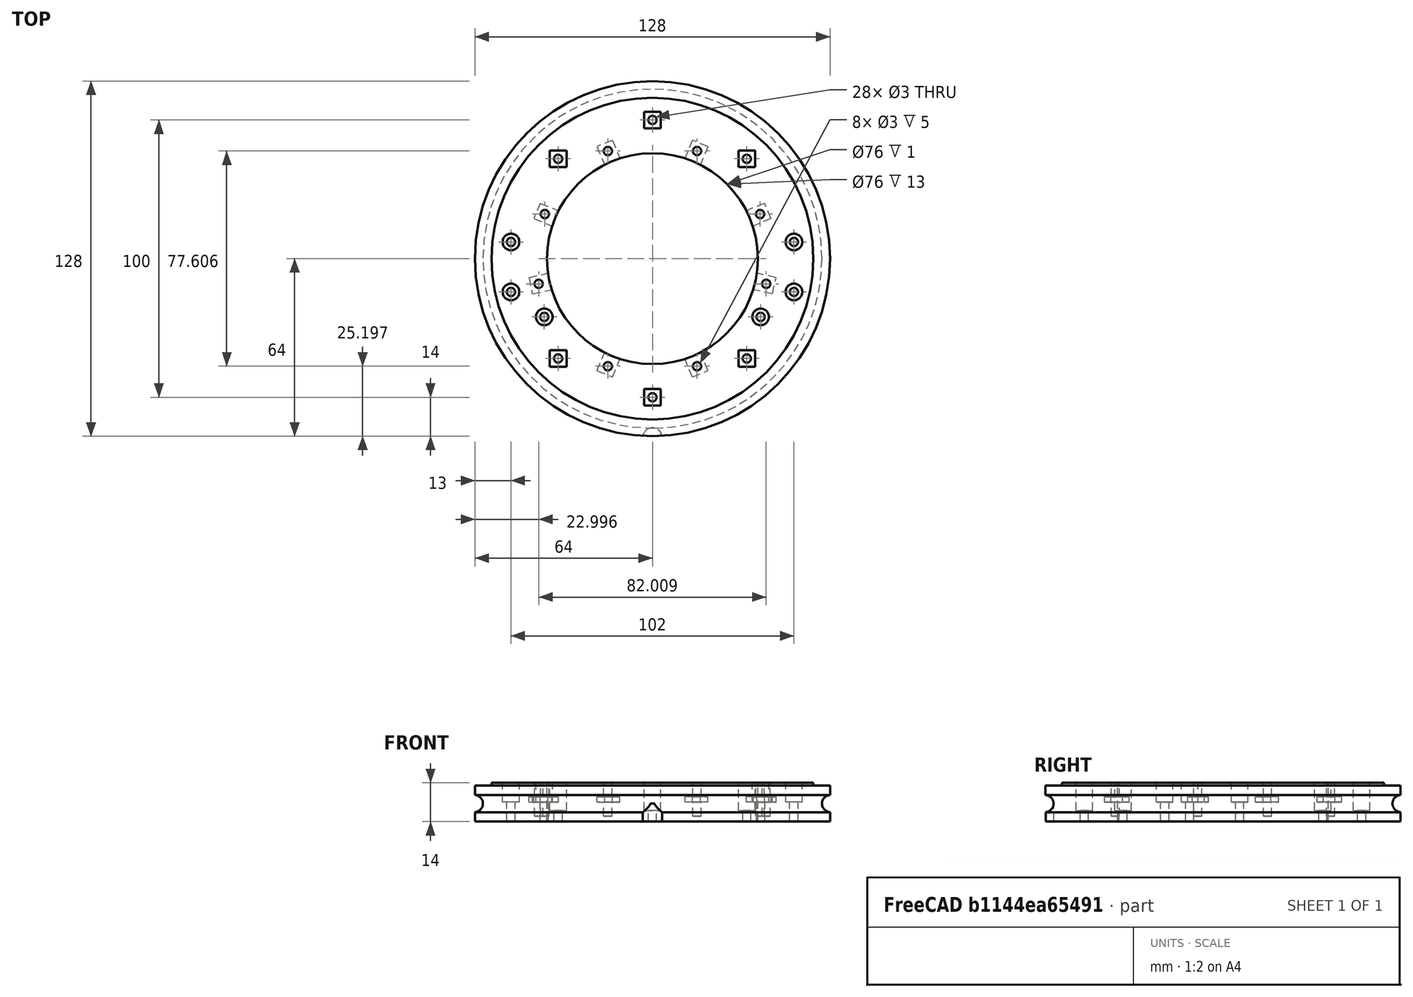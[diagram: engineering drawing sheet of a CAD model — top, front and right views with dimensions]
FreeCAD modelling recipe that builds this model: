
FCSTD DOCUMENT  (FreeCAD 0.19R24276 (Git))
Label: bazovina-part-C_loziskovina_008
License: All rights reserved
LicenseURL: http://en.wikipedia.org/wiki/All_rights_reserved
objects: Part::Cylinder×41, Part::Box×20, Part::Cut×13, Part::Compound×12, Part::FeaturePython×2, Part::Torus×1, Mesh::Feature×1
note: 89 computed .brp shape members not serialized (recipe doc carries the construction recipe); baked Part::Feature solids carry a one-line shape summary decoded from their .brp

FEATURE [Part::FeaturePython] Tube019  # WARN: FeaturePython — macro-defined, semantics opaque (R4)
  AttacherType = Attacher::AttachEngine3D
  Height = 13
  InnerRadius = 38
  OuterRadius = 64
  Placement = pos=(0,0,18) rot=(0,0,1;0rad)
FEATURE [Part::FeaturePython] Tube020  # WARN: FeaturePython — macro-defined, semantics opaque (R4)
  AttacherType = Attacher::AttachEngine3D
  Height = 1
  InnerRadius = 38
  OuterRadius = 58
  Placement = pos=(0,0,31) rot=(0,0,1;0rad)
FEATURE [Part::Torus] Torus  label="Anuloid"
  Angle1 = -180
  Angle2 = 180
  Angle3 = 360
  AttacherType = Attacher::AttachEngine3D
  Placement = pos=(0,0,24.5) rot=(0,0,1;0rad)
  Radius1 = 64.2
  Radius2 = 3.1
FEATURE [Part::Cut] Cut129
  Base = -> Tube019
  Tool = -> Torus
FEATURE [Part::Cylinder] Cylinder288  label="Válec288"
  Angle = 360
  AttacherType = Attacher::AttachEngine3D
  Height = 20
  Placement = pos=(0,-64.5,4.5) rot=(0,0,1;0rad)
  Radius = 3.5
FEATURE [Part::Cut] Cut130
  Base = -> Cut129
  Tool = -> Cylinder288
FEATURE [Part::Cylinder] Cylinder371  label="Válec371"
  Angle = 360
  AttacherType = Attacher::AttachEngine3D
  Height = 50
  Placement = pos=(34,36,0) rot=(0,0,1;0rad)
  Radius = 1.5
FEATURE [Part::Cylinder] Cylinder372  label="Válec372"
  Angle = 360
  AttacherType = Attacher::AttachEngine3D
  Height = 50
  Placement = pos=(-34,-36,0) rot=(0,0,1;0rad)
  Radius = 1.5
FEATURE [Part::Cylinder] Cylinder373  label="Válec373"
  Angle = 360
  AttacherType = Attacher::AttachEngine3D
  Height = 50
  Placement = pos=(34,-36,0) rot=(0,0,1;0rad)
  Radius = 1.5
FEATURE [Part::Cylinder] Cylinder370  label="Válec370"
  Angle = 360
  AttacherType = Attacher::AttachEngine3D
  Height = 50
  Placement = pos=(-34,36,0) rot=(0,0,1;0rad)
  Radius = 1.5
FEATURE [Part::Cylinder] Cylinder374  label="Válec374"
  Angle = 360
  AttacherType = Attacher::AttachEngine3D
  Height = 50
  Placement = pos=(0,50,0) rot=(0,0,1;0rad)
  Radius = 1.5
FEATURE [Part::Cylinder] Cylinder375  label="Válec375"
  Angle = 360
  AttacherType = Attacher::AttachEngine3D
  Height = 50
  Placement = pos=(0,-50,0) rot=(0,0,1;0rad)
  Radius = 1.5
FEATURE [Part::Cylinder] Cylinder376  label="Válec376"
  Angle = 360
  AttacherType = Attacher::AttachEngine3D
  Height = 100
  Placement = pos=(-51,-12,0) rot=(0,0,1;0rad)
  Radius = 1.5
FEATURE [Part::Cylinder] Cylinder377  label="Válec377"
  Angle = 360
  AttacherType = Attacher::AttachEngine3D
  Height = 50
  Placement = pos=(51,6,0) rot=(0,0,1;0rad)
  Radius = 1.5
FEATURE [Part::Cylinder] Cylinder409  label="Válec409"
  Angle = 360
  AttacherType = Attacher::AttachEngine3D
  Height = 7
  Placement = pos=(51,6,50) rot=(0,0,1;0rad)
  Radius = 3
FEATURE [Part::Cylinder] Cylinder404  label="Válec404"
  Angle = 360
  AttacherType = Attacher::AttachEngine3D
  Height = 7
  Placement = pos=(-51,6,50) rot=(0,0,1;0rad)
  Radius = 3
FEATURE [Part::Box] Box149  label="Krychle149"
  AttacherType = Attacher::AttachEngine3D
  Height = 10
  Length = 6
  Placement = pos=(-37,33,40) rot=(0,0,1;0rad)
  Width = 6
FEATURE [Part::Box] Box150  label="Krychle150"
  AttacherType = Attacher::AttachEngine3D
  Height = 10
  Length = 6
  Placement = pos=(31,-39,40) rot=(0,0,1;0rad)
  Width = 6
FEATURE [Part::Cylinder] Cylinder378  label="Válec378"
  Angle = 360
  AttacherType = Attacher::AttachEngine3D
  Height = 50
  Placement = pos=(-51,6,0) rot=(0,0,1;0rad)
  Radius = 1.5
FEATURE [Part::Cylinder] Cylinder379  label="Válec379"
  Angle = 360
  AttacherType = Attacher::AttachEngine3D
  Height = 100
  Placement = pos=(51,-12,0) rot=(0,0,1;0rad)
  Radius = 1.5
FEATURE [Part::Compound] Compound308
  Links = -> [Cylinder370,Cylinder371,Cylinder372,Cylinder373,Cylinder374,Cylinder375,Cylinder376,Cylinder377,Cylinder378,Cylinder379]
FEATURE [Part::Cut] Cut160
  Base = -> Cut130
  Tool = -> Compound308
FEATURE [Part::Cylinder] Cylinder411  label="Válec411"
  Angle = 360
  AttacherType = Attacher::AttachEngine3D
  Height = 7
  Placement = pos=(51,-12,50) rot=(0,0,1;0rad)
  Radius = 3
FEATURE [Part::Cylinder] Cylinder406  label="Válec406"
  Angle = 360
  AttacherType = Attacher::AttachEngine3D
  Height = 7
  Placement = pos=(-51,-12,50) rot=(0,0,1;0rad)
  Radius = 3
FEATURE [Part::Cylinder] Cylinder405  label="Válec405"
  Angle = 360
  AttacherType = Attacher::AttachEngine3D
  Height = 7
  Placement = pos=(51,6,50) rot=(0,0,1;0rad)
  Radius = 3
FEATURE [Part::Cylinder] Cylinder408  label="Válec408"
  Angle = 360
  AttacherType = Attacher::AttachEngine3D
  Height = 7
  Placement = pos=(-51,-12,50) rot=(0,0,1;0rad)
  Radius = 3
FEATURE [Part::Cylinder] Cylinder410  label="Válec410"
  Angle = 360
  AttacherType = Attacher::AttachEngine3D
  Height = 7
  Placement = pos=(-51,6,50) rot=(0,0,1;0rad)
  Radius = 3
FEATURE [Part::Compound] Compound313
  Links = -> [Cylinder408,Cylinder411,Cylinder409,Cylinder410]
  Placement = pos=(0,0,-25) rot=(0,0,1;0rad)
FEATURE [Part::Cut] Cut162
  Base = -> Cut160
  Tool = -> Compound313
FEATURE [Part::Box] Box145  label="Krychle145"
  AttacherType = Attacher::AttachEngine3D
  Height = 10
  Length = 6
  Placement = pos=(-3,47,40) rot=(0,0,1;0rad)
  Width = 6
FEATURE [Part::Box] Box146  label="Krychle146"
  AttacherType = Attacher::AttachEngine3D
  Height = 10
  Length = 6
  Placement = pos=(-3,-53,40) rot=(0,0,1;0rad)
  Width = 6
FEATURE [Part::Box] Box147  label="Krychle147"
  AttacherType = Attacher::AttachEngine3D
  Height = 10
  Length = 6
  Placement = pos=(-37,-39,40) rot=(0,0,1;0rad)
  Width = 6
FEATURE [Part::Box] Box148  label="Krychle148"
  AttacherType = Attacher::AttachEngine3D
  Height = 10
  Length = 6
  Placement = pos=(31,33,40) rot=(0,0,1;0rad)
  Width = 6
FEATURE [Part::Compound] Compound315
  Links = -> [Box145,Box147,Box146,Box148,Box149,Box150]
  Placement = pos=(0,0,-18) rot=(0,0,1;0rad)
FEATURE [Part::Cylinder] Cylinder407  label="Válec407"
  Angle = 360
  AttacherType = Attacher::AttachEngine3D
  Height = 7
  Placement = pos=(51,-12,50) rot=(0,0,1;0rad)
  Radius = 3
FEATURE [Part::Compound] Compound312
  Links = -> [Cylinder406,Cylinder407,Cylinder405,Cylinder404]
  Placement = pos=(0,0,-25) rot=(0,0,1;0rad)
FEATURE [Part::Cut] Cut161
  Base = -> Tube020
  Tool = -> Compound312
FEATURE [Part::Cut] Cut164
  Base = -> Cut162
  Tool = -> Compound315
FEATURE [Part::Box] Box151  label="Krychle151"
  AttacherType = Attacher::AttachEngine3D
  Height = 10
  Length = 6
  Placement = pos=(-3,-53,40) rot=(0,0,1;0rad)
  Width = 6
FEATURE [Part::Box] Box153  label="Krychle153"
  AttacherType = Attacher::AttachEngine3D
  Height = 10
  Length = 6
  Placement = pos=(-37,33,40) rot=(0,0,1;0rad)
  Width = 6
FEATURE [Part::Box] Box152  label="Krychle152"
  AttacherType = Attacher::AttachEngine3D
  Height = 10
  Length = 6
  Placement = pos=(-3,47,40) rot=(0,0,1;0rad)
  Width = 6
FEATURE [Part::Box] Box156  label="Krychle156"
  AttacherType = Attacher::AttachEngine3D
  Height = 10
  Length = 6
  Placement = pos=(31,-39,40) rot=(0,0,1;0rad)
  Width = 6
FEATURE [Part::Box] Box154  label="Krychle154"
  AttacherType = Attacher::AttachEngine3D
  Height = 10
  Length = 6
  Placement = pos=(-37,-39,40) rot=(0,0,1;0rad)
  Width = 6
FEATURE [Part::Box] Box155  label="Krychle155"
  AttacherType = Attacher::AttachEngine3D
  Height = 10
  Length = 6
  Placement = pos=(31,33,40) rot=(0,0,1;0rad)
  Width = 6
FEATURE [Part::Compound] Compound316
  Links = -> [Box152,Box154,Box151,Box155,Box153,Box156]
  Placement = pos=(0,0,-18) rot=(0,0,1;0rad)
FEATURE [Part::Cut] Cut163
  Base = -> Cut161
  Tool = -> Compound316
FEATURE [Part::Box] Box158  label="Krychle158"
  AttacherType = Attacher::AttachEngine3D
  Height = 2
  Length = 6
  Placement = pos=(43.284,-12.6687,25) rot=(0,0,1;1.35263rad)
  Width = 8
FEATURE [Part::Box] Box159  label="Krychle159"
  AttacherType = Attacher::AttachEngine3D
  Height = 2
  Length = 6
  Placement = pos=(42.7226,14.4491,25) rot=(0,0,1;1.96349rad)
  Width = 8
FEATURE [Part::Box] Box157  label="Krychle157"
  AttacherType = Attacher::AttachEngine3D
  Height = 2
  Length = 6
  Placement = pos=(14.4491,-42.7226,25) rot=(0,0,1;0.392699rad)
  Width = 8
FEATURE [Part::Box] Box162  label="Krychle162"
  AttacherType = Attacher::AttachEngine3D
  Height = 2
  Length = 6
  Placement = pos=(-40.4265,19.9924,25) rot=(0,0,-1;1.96349rad)
  Width = 8
FEATURE [Part::Box] Box160  label="Krychle160"
  AttacherType = Attacher::AttachEngine3D
  Height = 2
  Length = 6
  Placement = pos=(19.9924,40.4265,25) rot=(0,0,1;2.74889rad)
  Width = 8
FEATURE [Part::Box] Box164  label="Krychle164"
  AttacherType = Attacher::AttachEngine3D
  Height = 2
  Length = 6
  Placement = pos=(-19.9924,-40.4265,25) rot=(0,0,-1;0.392699rad)
  Width = 8
FEATURE [Part::Box] Box163  label="Krychle163"
  AttacherType = Attacher::AttachEngine3D
  Height = 2
  Length = 6
  Placement = pos=(-44.5826,-6.81089,25) rot=(0,0,-1;1.35263rad)
  Width = 8
FEATURE [Part::Cylinder] Cylinder444  label="Válec444"
  Angle = 360
  AttacherType = Attacher::AttachEngine3D
  Height = 100
  Placement = pos=(16.0727,-38.8029,0) rot=(0,0,1;0.785398rad)
  Radius = 1.5
FEATURE [Part::Box] Box161  label="Krychle161"
  AttacherType = Attacher::AttachEngine3D
  Height = 2
  Length = 6
  Placement = pos=(-14.4491,42.7226,25) rot=(0,0,1;3.53429rad)
  Width = 8
FEATURE [Part::Compound] Compound322
  Links = -> [Box157,Box158,Box159,Box160,Box161,Box162,Box163,Box164]
FEATURE [Part::Cylinder] Cylinder445  label="Válec445"
  Angle = 360
  AttacherType = Attacher::AttachEngine3D
  Height = 100
  Placement = pos=(41.0044,-9.09046,0) rot=(0,0,1;1.74533rad)
  Radius = 1.5
FEATURE [Part::Cylinder] Cylinder446  label="Válec446"
  Angle = 360
  AttacherType = Attacher::AttachEngine3D
  Height = 100
  Placement = pos=(38.8029,16.0727,0) rot=(0,0,1;2.35619rad)
  Radius = 1.5
FEATURE [Part::Cylinder] Cylinder450  label="Válec450"
  Angle = 360
  AttacherType = Attacher::AttachEngine3D
  Height = 100
  Placement = pos=(-41.0044,-9.09046,0) rot=(0,0,-1;0.959931rad)
  Radius = 1.5
FEATURE [Part::Cylinder] Cylinder448  label="Válec448"
  Angle = 360
  AttacherType = Attacher::AttachEngine3D
  Height = 100
  Placement = pos=(-16.0727,38.8029,0) rot=(0,0,1;3.92699rad)
  Radius = 1.5
FEATURE [Part::Cylinder] Cylinder447  label="Válec447"
  Angle = 360
  AttacherType = Attacher::AttachEngine3D
  Height = 100
  Placement = pos=(16.0727,38.8029,0) rot=(0,0,1;3.14159rad)
  Radius = 1.5
FEATURE [Part::Cylinder] Cylinder449  label="Válec449"
  Angle = 360
  AttacherType = Attacher::AttachEngine3D
  Height = 100
  Placement = pos=(-38.8029,16.0727,0) rot=(0,0,-1;1.5708rad)
  Radius = 1.5
FEATURE [Part::Cylinder] Cylinder451  label="Válec451"
  Angle = 360
  AttacherType = Attacher::AttachEngine3D
  Height = 100
  Placement = pos=(-16.0727,-38.8029,0) rot=(0,0,1;0rad)
  Radius = 1.5
FEATURE [Part::Compound] Compound325
  Links = -> [Cylinder444,Cylinder445,Cylinder446,Cylinder447,Cylinder448,Cylinder449,Cylinder450,Cylinder451]
FEATURE [Part::Cut] Cut173
  Base = -> Cut163
  Tool = -> Compound325
FEATURE [Part::Cylinder] Cylinder471  label="Válec471"
  Angle = 360
  AttacherType = Attacher::AttachEngine3D
  Height = 100
  Placement = pos=(16.0727,38.8029,0) rot=(0,0,1;3.14159rad)
  Radius = 1.5
FEATURE [Part::Cylinder] Cylinder468  label="Válec468"
  Angle = 360
  AttacherType = Attacher::AttachEngine3D
  Height = 100
  Placement = pos=(16.0727,-38.8029,0) rot=(0,0,1;0.785398rad)
  Radius = 1.5
FEATURE [Part::Cylinder] Cylinder473  label="Válec473"
  Angle = 360
  AttacherType = Attacher::AttachEngine3D
  Height = 100
  Placement = pos=(-38.8029,16.0727,0) rot=(0,0,-1;1.5708rad)
  Radius = 1.5
FEATURE [Part::Cylinder] Cylinder474  label="Válec474"
  Angle = 360
  AttacherType = Attacher::AttachEngine3D
  Height = 100
  Placement = pos=(-41.0044,-9.09046,0) rot=(0,0,-1;0.959931rad)
  Radius = 1.5
FEATURE [Part::Cylinder] Cylinder475  label="Válec475"
  Angle = 360
  AttacherType = Attacher::AttachEngine3D
  Height = 100
  Placement = pos=(-16.0727,-38.8029,0) rot=(0,0,1;0rad)
  Radius = 1.5
FEATURE [Part::Cylinder] Cylinder470  label="Válec470"
  Angle = 360
  AttacherType = Attacher::AttachEngine3D
  Height = 100
  Placement = pos=(38.8029,16.0727,0) rot=(0,0,1;2.35619rad)
  Radius = 1.5
FEATURE [Part::Cylinder] Cylinder469  label="Válec469"
  Angle = 360
  AttacherType = Attacher::AttachEngine3D
  Height = 100
  Placement = pos=(41.0044,-9.09046,0) rot=(0,0,1;1.74533rad)
  Radius = 1.5
FEATURE [Part::Cylinder] Cylinder472  label="Válec472"
  Angle = 360
  AttacherType = Attacher::AttachEngine3D
  Height = 100
  Placement = pos=(-16.0727,38.8029,0) rot=(0,0,1;3.92699rad)
  Radius = 1.5
FEATURE [Part::Compound] Compound328
  Links = -> [Cylinder468,Cylinder469,Cylinder470,Cylinder471,Cylinder472,Cylinder473,Cylinder474,Cylinder475]
  Placement = pos=(0,0,20) rot=(0,0,1;0rad)
FEATURE [Part::Cut] Cut174
  Base = -> Cut164
  Tool = -> Compound328
FEATURE [Part::Cut] Cut175
  Base = -> Cut174
  Tool = -> Compound322
FEATURE [Part::Cylinder] Cylinder528  label="Válec528"
  Angle = 360
  AttacherType = Attacher::AttachEngine3D
  Height = 100
  Placement = pos=(-39,-21,0) rot=(0,0,1;0rad)
  Radius = 1.5
FEATURE [Part::Cylinder] Cylinder529  label="Válec529"
  Angle = 360
  AttacherType = Attacher::AttachEngine3D
  Height = 100
  Placement = pos=(39,-21,0) rot=(0,0,1;0rad)
  Radius = 1.5
FEATURE [Part::Compound] Compound
  Links = -> [Cylinder528,Cylinder529]
FEATURE [Part::Cylinder] Cylinder530  label="Válec530"
  Angle = 360
  AttacherType = Attacher::AttachEngine3D
  Height = 7
  Placement = pos=(-39,-21,50) rot=(0,0,1;0rad)
  Radius = 3
FEATURE [Part::Cylinder] Cylinder531  label="Válec531"
  Angle = 360
  AttacherType = Attacher::AttachEngine3D
  Height = 7
  Placement = pos=(39,-21,50) rot=(0,0,1;0rad)
  Radius = 3
FEATURE [Part::Compound] Compound337
  Links = -> [Cylinder530,Cylinder531]
  Placement = pos=(0,0,-25) rot=(0,0,1;0rad)
FEATURE [Part::Cut] Cut
  Base = -> Cut173
  Tool = -> Compound337
FEATURE [Part::Cylinder] Cylinder532  label="Válec532"
  Angle = 360
  AttacherType = Attacher::AttachEngine3D
  Height = 7
  Placement = pos=(-39,-21,50) rot=(0,0,1;0rad)
  Radius = 3
FEATURE [Part::Cylinder] Cylinder533  label="Válec533"
  Angle = 360
  AttacherType = Attacher::AttachEngine3D
  Height = 7
  Placement = pos=(39,-21,50) rot=(0,0,1;0rad)
  Radius = 3
FEATURE [Part::Compound] Compound338
  Links = -> [Cylinder532,Cylinder533]
  Placement = pos=(0,0,-25) rot=(0,0,1;0rad)
FEATURE [Part::Cut] Cut176
  Base = -> Cut175
  Tool = -> Compound338
FEATURE [Part::Cut] Cut177
  Base = -> Cut176
  Tool = -> Compound
FEATURE [Part::Compound] Compound339  label="bazovina-part-C_loziskovina"
  Links = -> [Cut,Cut177]
FEATURE [Mesh::Feature] Mesh  label="bazovina-part-C_loziskovina (Meshed)"
